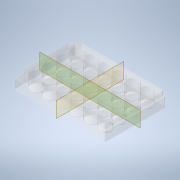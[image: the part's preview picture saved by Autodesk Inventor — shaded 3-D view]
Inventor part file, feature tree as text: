
AUTODESK INVENTOR PART (.ipt)
format: ipt  version: 2022 (Build 260153000, 153)  size: 250,368 bytes
history: native  units: mm
features: plane x2, other x1
ambient origin geometry x8: Origin, YZ Plane, XZ Plane, XY Plane, X Axis, Y Axis, Z Axis, Center Point
bodies: Solid1 (feature_tree)
feature tree (3):
  plane  "Arbeitsebene1"
  plane  "Arbeitsebene2"
  other  "Plate Edge Fillets"
